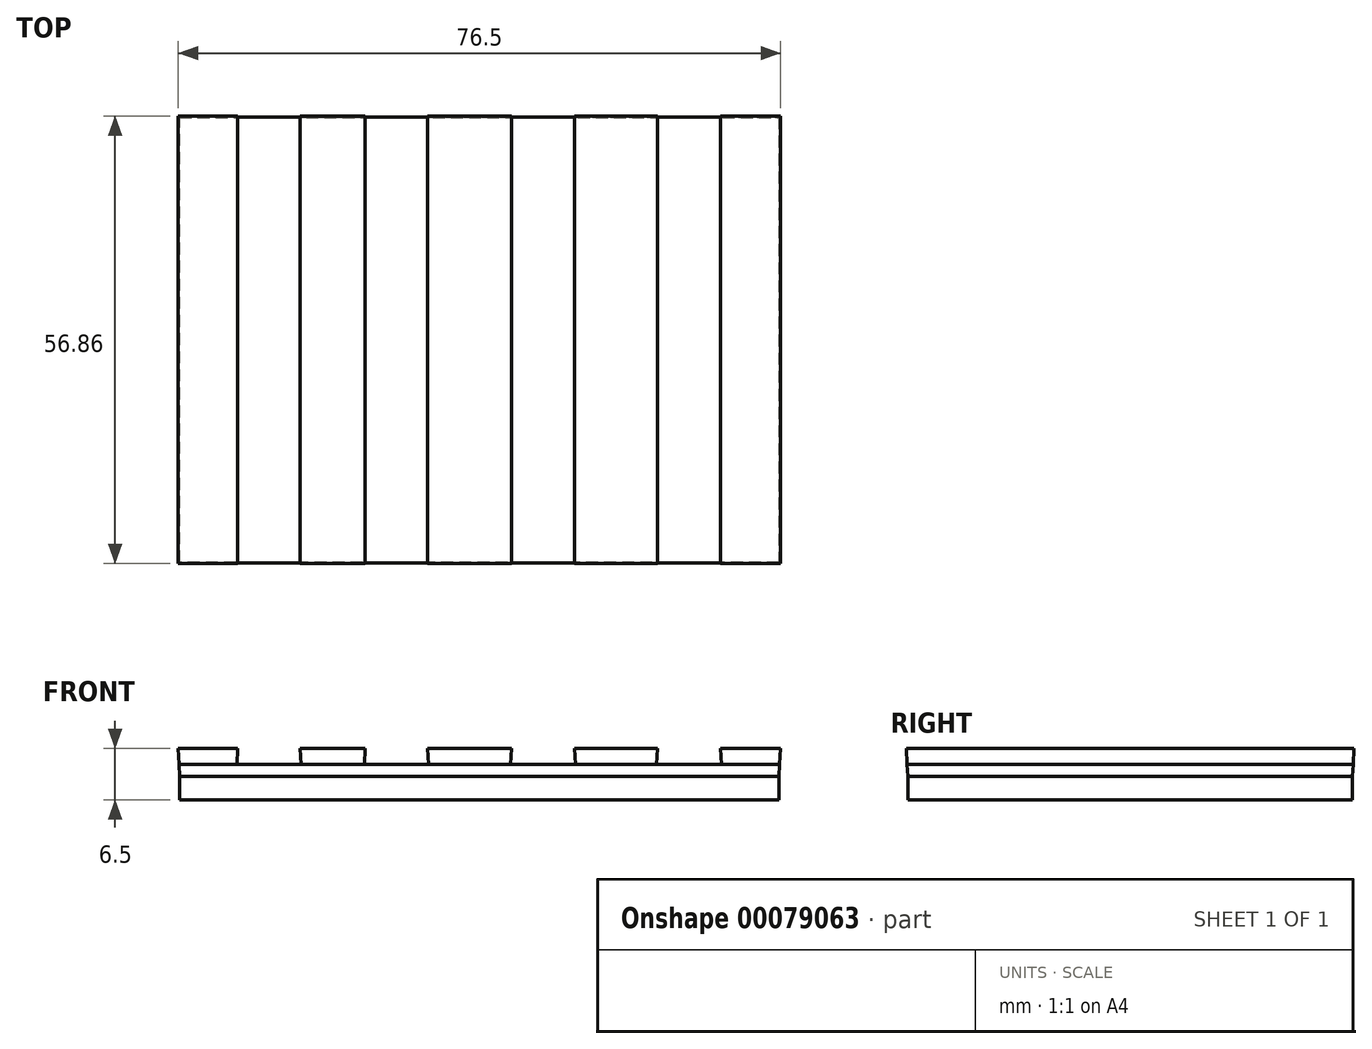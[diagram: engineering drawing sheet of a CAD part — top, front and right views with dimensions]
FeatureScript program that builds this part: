
annotation { "Feature Type Name" : "Feature", "Feature Type Description" : "" }
export const myFeature = defineFeature(function(context is Context, id is Id, definition is map)
    precondition{}
    {
        {
            var Q0;
            Q0=qCreatedBy(makeId("Top.planeOp"),FACE);
            var sketch = newSketch(context, id + "F0", { "sketchPlane" : qUnion([Q0])});
            skLineSegment(sketch, "E0.bottom", {"start": v(-76.14, 56.5) * mm, "end": v(0, 56.5) * mm});
            skLineSegment(sketch, "E0.top", {"start": v(-76.14, 0) * mm, "end": v(0, 0) * mm});
            skLineSegment(sketch, "E0.left", {"start": v(-76.14, 56.5) * mm, "end": v(-76.14, 0) * mm});
            skLineSegment(sketch, "E0.right", {"start": v(0, 56.5) * mm, "end": v(0, 0) * mm});
            skSolve(sketch);
        }
        {
            var Q0;
            Q0=qSketchRegion(id+"F0",true);
            extrude(context, id + "F1", {"entities" : qUnion([Q0]), "depth" : 3 * mm});
        }
        {
            var Q0;
            Q0=makeQuery(id+"F1.opExtrude","CAP_FACE",FACE,{"disambiguationData":[OSD([sQuery(id+"F0.wireOp",EDGE,"E0.bottom"),sQuery(id+"F0.wireOp",EDGE,"E0.top"),sQuery(id+"F0.wireOp",EDGE,"E0.left"),sQuery(id+"F0.wireOp",EDGE,"E0.right")])],"isStart":false});
            var sketch = newSketch(context, id + "F2", { "sketchPlane" : qUnion([Q0])});
            skLineSegment(sketch, "E1.bottom", {"start": v(-76.14, 56.5) * mm, "end": v(0, 56.5) * mm});
            skLineSegment(sketch, "E1.top", {"start": v(-76.14, 0) * mm, "end": v(0, 0) * mm});
            skLineSegment(sketch, "E1.left", {"start": v(-76.14, 56.5) * mm, "end": v(-76.14, 0) * mm});
            skLineSegment(sketch, "E1.right", {"start": v(0, 56.5) * mm, "end": v(0, 0) * mm});
            skSolve(sketch);
        }
        {
            var Q0;
            Q0=makeQuery(id+"F2.imprint","IMPRINT",FACE,{"disambiguationData":[TD([[makeQuery(id+"F2.imprint","IMPRINT",EDGE,{"derivedFrom":sQuery(id+"F2.wireOp",EDGE,"E1.bottom")}),-1.0]])]});
            extrude(context, id + "F3", {"entities" : qUnion([Q0]), "depth" : 1.5 * mm, "hasDraft" : true, "draftAngle" : 3 * degree});
        }
        {
            var Q0;
            Q0=makeQuery(id+"F3.opExtrude","CAP_FACE",FACE,{"disambiguationData":[OSD([sQuery(id+"F2.wireOp",EDGE,"E1.bottom"),sQuery(id+"F2.wireOp",EDGE,"E1.top"),sQuery(id+"F2.wireOp",EDGE,"E1.left"),sQuery(id+"F2.wireOp",EDGE,"E1.right")])],"isStart":false});
            var sketch = newSketch(context, id + "F4", { "sketchPlane" : qUnion([Q0])});
            skLineSegment(sketch, "E2.bottom", {"start": v(-76.22, 56.58) * mm, "end": v(0.08, 56.58) * mm});
            skLineSegment(sketch, "E2.top", {"start": v(-76.22, -0.08) * mm, "end": v(0.08, -0.08) * mm});
            skLineSegment(sketch, "E2.left", {"start": v(-76.22, 56.58) * mm, "end": v(-76.22, -0.08) * mm});
            skLineSegment(sketch, "E2.right", {"start": v(0.08, 56.58) * mm, "end": v(0.08, -0.08) * mm});
            skSolve(sketch);
        }
        {
            var Q0;
            Q0=qSketchRegion(id+"F4",true);
            extrude(context, id + "F5", {"entities" : qUnion([Q0]), "depth" : 2 * mm, "hasDraft" : true, "draftAngle" : 3 * degree});
        }
        {
            var Q0;
            Q0=makeQuery(id+"F5.opExtrude","CAP_FACE",FACE,{"disambiguationData":[OSD([sQuery(id+"F4.wireOp",EDGE,"E2.bottom"),sQuery(id+"F4.wireOp",EDGE,"E2.top"),sQuery(id+"F4.wireOp",EDGE,"E2.left"),sQuery(id+"F4.wireOp",EDGE,"E2.right")])],"isStart":false});
            var sketch = newSketch(context, id + "F6", { "sketchPlane" : qUnion([Q0])});
            skLineSegment(sketch, "E3.bottom", {"start": v(-68.76, 56.68) * mm, "end": v(-60.82, 56.68) * mm});
            skLineSegment(sketch, "E3.top", {"start": v(-68.76, -0.18) * mm, "end": v(-60.82, -0.18) * mm});
            skLineSegment(sketch, "E3.left", {"start": v(-68.76, 56.68) * mm, "end": v(-68.76, -0.18) * mm});
            skLineSegment(sketch, "E3.right", {"start": v(-60.82, 56.68) * mm, "end": v(-60.82, -0.18) * mm});
            skSolve(sketch);
        }
        {
            var Q0;
            Q0 = qSketchRegion(id + "F6", true);
            extrude(context, id + "F7", {"entities" : qUnion([Q0]), "operationType" : NewBodyOperationType.REMOVE, "oppositeDirection" : true, "depth" : 2 * mm, "hasDraft" : true, "draftAngle" : 3 * degree});
        }
        {
            var Q0;
            {var subQ0=sQuery(id+"F4.wireOp",EDGE,"E2.bottom");var subQ1=sQuery(id+"F4.wireOp",EDGE,"E2.top");var subQ2=sQuery(id+"F4.wireOp",EDGE,"E2.right");Q0=makeQuery(id+"F7.boolean.opBoolean","SPLIT",FACE,{"disambiguationData":[TD([makeQuery(id+"F5.opExtrude","SWEPT_FACE",FACE,{"disambiguationData":[OSD([subQ2])]})])],"derivedFrom":makeQuery(id+"F5.opExtrude","CAP_FACE",FACE,{"disambiguationData":[OSD([subQ0,subQ1,sQuery(id+"F4.wireOp",EDGE,"E2.left"),subQ2])],"isStart":false})});}
            var sketch = newSketch(context, id + "F8", { "sketchPlane" : qUnion([Q0])});
            skLineSegment(sketch, "E4.bottom", {"start": v(-52.56, 56.68) * mm, "end": v(-44.62, 56.68) * mm});
            skLineSegment(sketch, "E4.top", {"start": v(-52.56, -0.18) * mm, "end": v(-44.62, -0.18) * mm});
            skLineSegment(sketch, "E4.left", {"start": v(-52.56, 56.68) * mm, "end": v(-52.56, -0.18) * mm});
            skLineSegment(sketch, "E4.right", {"start": v(-44.62, 56.68) * mm, "end": v(-44.62, -0.18) * mm});
            skSolve(sketch);
        }
        {
            var Q0;
            Q0 = qSketchRegion(id + "F8", true);
            extrude(context, id + "F9", {"entities" : qUnion([Q0]), "operationType" : NewBodyOperationType.REMOVE, "oppositeDirection" : true, "depth" : 2 * mm, "hasDraft" : true, "draftAngle" : 3 * degree});
        }
        {
            var Q0;
            {var subQ0=sQuery(id+"F4.wireOp",EDGE,"E2.bottom");var subQ2=sQuery(id+"F4.wireOp",EDGE,"E2.top");var subQ4=sQuery(id+"F4.wireOp",EDGE,"E2.right");var subQ5=makeQuery(id+"F5.opExtrude","SWEPT_FACE",FACE,{"disambiguationData":[OSD([subQ4])]});Q0=makeQuery(id+"F9.boolean.opBoolean","SPLIT",FACE,{"disambiguationData":[TD([subQ5])],"derivedFrom":makeQuery(id+"F7.boolean.opBoolean","SPLIT",FACE,{"disambiguationData":[TD([subQ5])],"derivedFrom":makeQuery(id+"F5.opExtrude","CAP_FACE",FACE,{"disambiguationData":[OSD([subQ0,subQ2,sQuery(id+"F4.wireOp",EDGE,"E2.left"),subQ4])],"isStart":false})})});}
            var sketch = newSketch(context, id + "F10", { "sketchPlane" : qUnion([Q0])});
            skLineSegment(sketch, "E5.bottom", {"start": v(-34, 56.68) * mm, "end": v(-25.99, 56.68) * mm});
            skLineSegment(sketch, "E5.top", {"start": v(-34, -0.18) * mm, "end": v(-25.99, -0.18) * mm});
            skLineSegment(sketch, "E5.left", {"start": v(-34, 56.68) * mm, "end": v(-34, -0.18) * mm});
            skLineSegment(sketch, "E5.right", {"start": v(-25.99, 56.68) * mm, "end": v(-25.99, -0.18) * mm});
            skSolve(sketch);
        }
        {
            var Q0;
            Q0 = qSketchRegion(id + "F10", true);
            extrude(context, id + "F11", {"entities" : qUnion([Q0]), "operationType" : NewBodyOperationType.REMOVE, "oppositeDirection" : true, "depth" : 2 * mm, "hasDraft" : true, "draftAngle" : 3 * degree});
        }
        {
            var Q0;
            {var subQ0=sQuery(id+"F4.wireOp",EDGE,"E2.bottom");var subQ2=sQuery(id+"F4.wireOp",EDGE,"E2.top");var subQ4=sQuery(id+"F4.wireOp",EDGE,"E2.right");var subQ5=makeQuery(id+"F5.opExtrude","SWEPT_FACE",FACE,{"disambiguationData":[OSD([subQ4])]});Q0=makeQuery(id+"F11.boolean.opBoolean","SPLIT",FACE,{"disambiguationData":[TD([subQ5])],"derivedFrom":makeQuery(id+"F9.boolean.opBoolean","SPLIT",FACE,{"disambiguationData":[TD([subQ5])],"derivedFrom":makeQuery(id+"F7.boolean.opBoolean","SPLIT",FACE,{"disambiguationData":[TD([subQ5])],"derivedFrom":makeQuery(id+"F5.opExtrude","CAP_FACE",FACE,{"disambiguationData":[OSD([subQ0,subQ2,sQuery(id+"F4.wireOp",EDGE,"E2.left"),subQ4])],"isStart":false})})})});}
            var sketch = newSketch(context, id + "F12", { "sketchPlane" : qUnion([Q0])});
            skLineSegment(sketch, "E6.bottom", {"start": v(-15.44, 56.68) * mm, "end": v(-7.42, 56.68) * mm});
            skLineSegment(sketch, "E6.top", {"start": v(-15.44, -0.18) * mm, "end": v(-7.42, -0.18) * mm});
            skLineSegment(sketch, "E6.left", {"start": v(-15.44, 56.68) * mm, "end": v(-15.44, -0.18) * mm});
            skLineSegment(sketch, "E6.right", {"start": v(-7.42, 56.68) * mm, "end": v(-7.42, -0.18) * mm});
            skSolve(sketch);
        }
        {
            var Q0;
            Q0 = qSketchRegion(id + "F12", true);
            extrude(context, id + "F13", {"entities" : qUnion([Q0]), "operationType" : NewBodyOperationType.REMOVE, "oppositeDirection" : true, "depth" : 2 * mm, "hasDraft" : true, "draftAngle" : 3 * degree});
        }
    });
